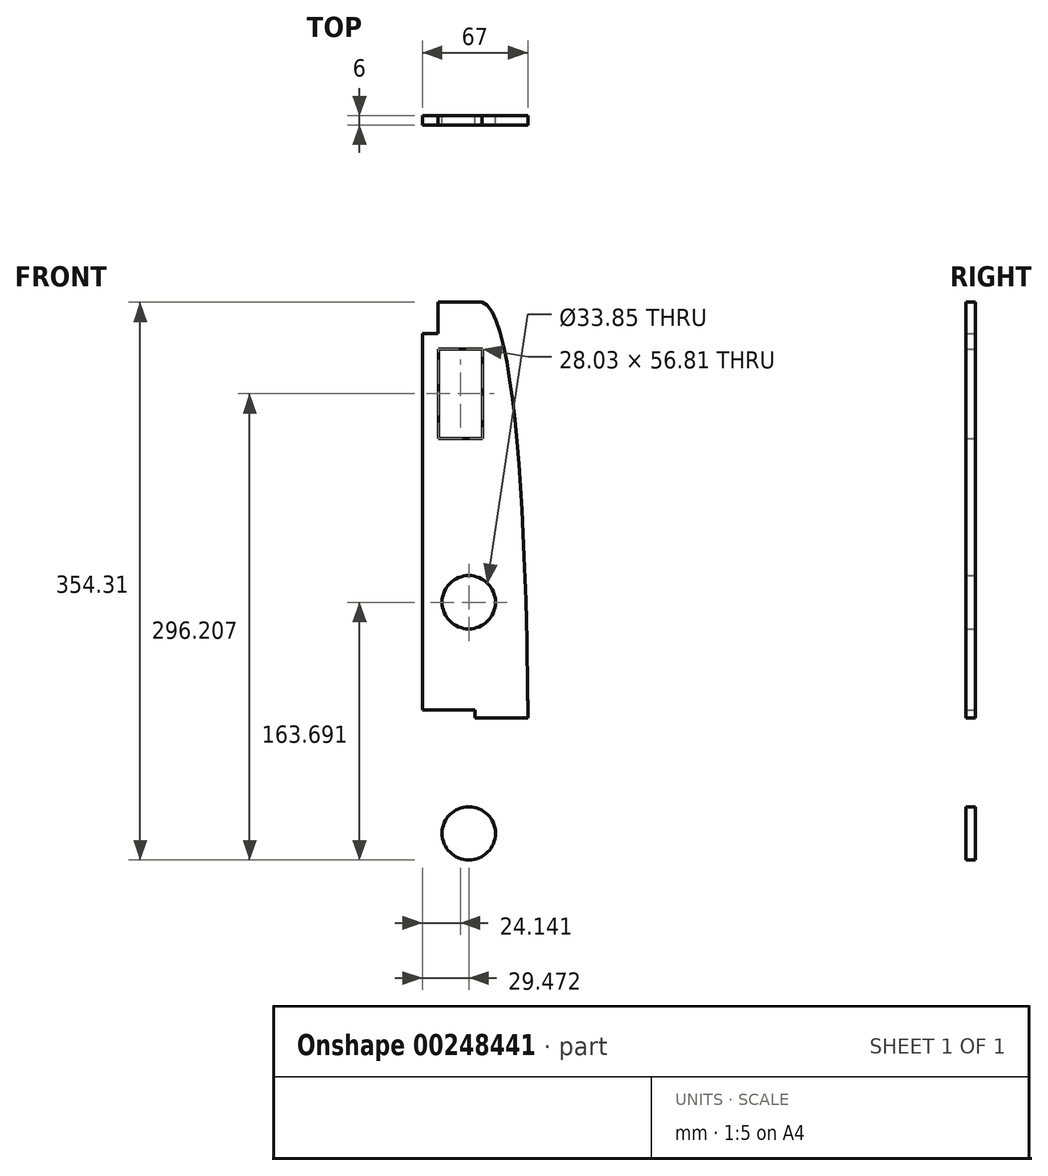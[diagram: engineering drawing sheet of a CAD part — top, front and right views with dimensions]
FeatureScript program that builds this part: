
annotation { "Feature Type Name" : "Feature", "Feature Type Description" : "" }
export const myFeature = defineFeature(function(context is Context, id is Id, definition is map)
    precondition{}
    {
        {
            var Q0;
            Q0=qCreatedBy(makeId("Front.planeOp"),FACE);
            var sketch = newSketch(context, id + "F0", { "sketchPlane" : qUnion([Q0])});
            skLineSegment(sketch, "E0.top", {"start": v(210.27, 259) * mm, "end": v(153.35, 259) * mm});
            skFitSpline(sketch, "E1", {"points": [v(181.35, 259) * mm, v(210.35, -5) * mm], "startDerivative": vector(86.73, -24) * mm, "endDerivative": vector(0.27, -3.02) * mm});
            skLineSegment(sketch, "E2", {"start": v(210.35, -5) * mm, "end": v(143.35, -5) * mm});
            skLineSegment(sketch, "E3", {"start": v(210.27, 259) * mm, "end": v(210.27, -4) * mm});
            skLineSegment(sketch, "E4.bottom", {"start": v(181.5, 229.3) * mm, "end": v(153.48, 229.3) * mm});
            skLineSegment(sketch, "E4.top", {"start": v(181.5, 172.5) * mm, "end": v(153.48, 172.5) * mm});
            skLineSegment(sketch, "E4.left", {"start": v(181.5, 229.3) * mm, "end": v(181.5, 172.5) * mm});
            skLineSegment(sketch, "E4.right", {"start": v(153.48, 229.3) * mm, "end": v(153.48, 172.5) * mm});
            skCircle(sketch, "E5", {"center": v(172.82, 68.38) * mm, "radius": 16.93 * mm});
            skCircle(sketch, "E6.MirrorC", {"center": v(172.82, -78.38) * mm, "radius": 16.93 * mm});
            skLineSegment(sketch, "E7.MirrorCS", {"start": v(181.5, -239.3) * mm, "end": v(181.5, -182.5) * mm});
            skLineSegment(sketch, "E8.MirrorCS", {"start": v(210.27, -269) * mm, "end": v(210.27, -6) * mm});
            skLineSegment(sketch, "E9.MirrorCS", {"start": v(181.5, -239.3) * mm, "end": v(153.48, -239.3) * mm});
            skLineSegment(sketch, "E10.MirrorCS", {"start": v(210.27, -269) * mm, "end": v(153.35, -269) * mm});
            skFitSpline(sketch, "E11.MirrorCS", {"points": [v(181.35, -269) * mm, v(210.35, -5) * mm], "startDerivative": vector(86.73, 24) * mm, "endDerivative": vector(0.27, 3.02) * mm});
            skLineSegment(sketch, "E12.MirrorCS", {"start": v(153.48, -239.3) * mm, "end": v(153.48, -182.5) * mm});
            skLineSegment(sketch, "E13.MirrorCS", {"start": v(181.5, -182.5) * mm, "end": v(153.48, -182.5) * mm});
            skLineSegment(sketch, "E14", {"start": v(176.85, -5) * mm, "end": v(176.85, 0) * mm});
            skLineSegment(sketch, "E15", {"start": v(176.85, -5) * mm, "end": v(176.85, -10) * mm});
            skLineSegment(sketch, "E16", {"start": v(176.85, 0) * mm, "end": v(143.35, 0) * mm});
            skLineSegment(sketch, "E17", {"start": v(176.85, -10) * mm, "end": v(143.35, -10) * mm});
            skLineSegment(sketch, "E18", {"start": v(153.35, 259) * mm, "end": v(153.35, 239) * mm});
            skLineSegment(sketch, "E19", {"start": v(153.35, 239) * mm, "end": v(143.35, 239) * mm});
            skLineSegment(sketch, "E20", {"start": v(153.35, 259) * mm, "end": v(181.35, 259) * mm});
            skLineSegment(sketch, "E21", {"start": v(143.35, 239) * mm, "end": v(143.35, 239) * mm});
            skLineSegment(sketch, "E22", {"start": v(143.35, 239) * mm, "end": v(143.35, 0) * mm});
            skLineSegment(sketch, "E23.MirrorCS", {"start": v(153.35, -269) * mm, "end": v(153.35, -249) * mm});
            skLineSegment(sketch, "E24.MirrorCS", {"start": v(153.35, -249) * mm, "end": v(143.35, -249) * mm});
            skLineSegment(sketch, "E25", {"start": v(153.35, -269) * mm, "end": v(181.35, -269) * mm});
            skLineSegment(sketch, "E26", {"start": v(143.35, -249) * mm, "end": v(143.35, -5) * mm});
            skSolve(sketch);
        }
        {
            var Q0;
            {var subQ3=sQuery(id+"F0.wireOp",EDGE,"22ec6738-759d-4b5e-af14-6f44bb41974b");Q0=makeQuery(id+"F0.imprint","IMPRINT",FACE,{"disambiguationData":[TD([[makeQuery(id+"F0.imprint","IMPRINT",EDGE,{"derivedFrom":subQ3}),-1.0]])]});}
            var Q1;
            Q1=makeQuery(id+"F0.imprint","IMPRINT",FACE,{"disambiguationData":[TD([[makeQuery(id+"F0.imprint","IMPRINT",EDGE,{"derivedFrom":sQuery(id+"F0.wireOp",EDGE,"E6.MirrorC")}),1.0]])]});
            var Q2;
            Q2=makeQuery(id+"F0.imprint","IMPRINT",FACE,{"disambiguationData":[TD([[makeQuery(id+"F0.imprint","IMPRINT",EDGE,{"derivedFrom":sQuery(id+"F0.wireOp",EDGE,"E4.bottom")}),-1.0]])]});
            extrude(context, id + "F1", {"entities" : qUnion([Q0, Q1, Q2]), "depth" : 6 * mm});
        }
    });
